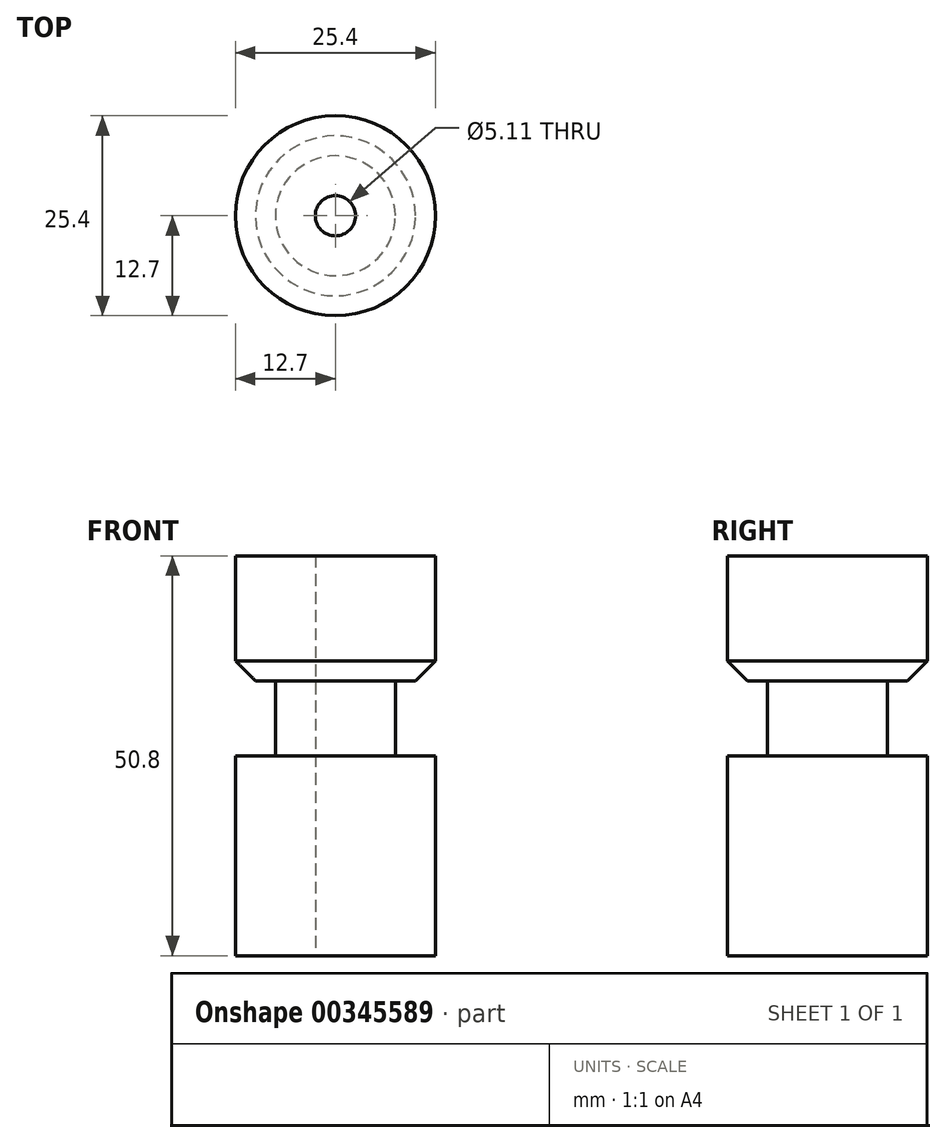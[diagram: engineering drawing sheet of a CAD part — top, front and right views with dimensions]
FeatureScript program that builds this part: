
annotation { "Feature Type Name" : "Feature", "Feature Type Description" : "" }
export const myFeature = defineFeature(function(context is Context, id is Id, definition is map)
    precondition{}
    {
        {
            var Q0;
            Q0=qCreatedBy(makeId("Top.planeOp"),FACE);
            var sketch = newSketch(context, id + "F0", { "sketchPlane" : qUnion([Q0])});
            skCircle(sketch, "E0", {"center": v(0, 0) * mm, "radius": 12.7 * mm});
            skSolve(sketch);
        }
        {
            var Q0;
            Q0 = qSketchRegion(id + "F0", true);
            extrude(context, id + "F1", {"entities" : qUnion([Q0]), "depth" : 50.8 * mm});
        }
        {
            var Q0;
            Q0=qCreatedBy(makeId("Right.planeOp"),FACE);
            var sketch = newSketch(context, id + "F2", { "sketchPlane" : qUnion([Q0])});
            skLineSegment(sketch, "E1.bottom", {"start": v(-7.62, 25.4) * mm, "end": v(-12.7, 25.4) * mm});
            skLineSegment(sketch, "E1.top", {"start": v(-7.62, 34.93) * mm, "end": v(-12.7, 34.93) * mm});
            skLineSegment(sketch, "E1.left", {"start": v(-7.62, 25.4) * mm, "end": v(-7.62, 34.93) * mm});
            skLineSegment(sketch, "E1.right", {"start": v(-12.7, 25.4) * mm, "end": v(-12.7, 34.93) * mm});
            skLineSegment(sketch, "E2", {"start": v(0, 0) * mm, "end": v(-30.16, 0) * mm});
            skLineSegment(sketch, "E3", {"start": v(-30.16, 0) * mm, "end": v(0, 0) * mm});
            skLineSegment(sketch, "E4", {"start": v(0, 102.3) * mm, "end": v(0, 0) * mm});
            skSolve(sketch);
        }
        {
            var Q0;
            Q0 = qSketchRegion(id + "F2", true);
            var Q1;
            Q1=sQuery(id+"F2.wireOp",EDGE,"E4");
            revolve(context, id + "F3", {"operationType" : NewBodyOperationType.REMOVE, "entities" : qUnion([Q0]), "axis" : qUnion([Q1]), "revolveType" : RevolveType.FULL, "oppositeDirection" : true});
        }
        {
            var Q0;
            Q0=makeQuery(id+"F3.boolean.opBoolean","COPY",EDGE,{"derivedFrom":makeQuery(id+"F3.opRevolve","SWEPT_EDGE",EDGE,{"disambiguationData":[OSD([sQuery(id+"F2.wireOp",EDGE,"E1.bottom"),sQuery(id+"F2.wireOp",EDGE,"E1.right")])]})});
            var Q1;
            Q1=makeQuery(id+"F3.boolean.opBoolean","COPY",EDGE,{"derivedFrom":makeQuery(id+"F3.opRevolve","SWEPT_EDGE",EDGE,{"disambiguationData":[OSD([sQuery(id+"F2.wireOp",EDGE,"E1.top"),sQuery(id+"F2.wireOp",EDGE,"E1.right")])]})});
            chamfer(context, id + "F4", {"entities" : qUnion([Q0, Q1]), "width" : 2.54 * mm, "tangentPropagation" : true});
        }
        {
            var Q0;
            Q0=qCreatedBy(makeId("Top.planeOp"),FACE);
            var sketch = newSketch(context, id + "F5", { "sketchPlane" : qUnion([Q0])});
            skPoint(sketch, "E5", {"position": v(0, 0) * mm});
            skSolve(sketch);
        }
        {
            var Q0;
            Q0=sQuery(id+"F5.wireOp",VERTEX,"E5");
            var Q1;
            Q1=makeQuery(id+"F1.opExtrude","SWEPT_BODY",BODY,{"disambiguationData":[OSD([sQuery(id+"F0.wireOp",EDGE,"E0")])]});
            hole(context, id + "F6", {"style" : HoleStyle.SIMPLE, "endStyle" : HoleEndStyle.THROUGH, "oppositeDirection" : true, "standardTappedOrClearance" : lookupTablePath({ "standard" : "ANSI", "fit" : "Normal (ASME)", "engagement" : "75%", "pitch" : "20 tpi", "size" : "1/4", "type" : "Tapped" }), "standardBlindInLast" : lookupTablePath({ "fit" : "Free", "standard" : "ANSI", "engagement" : "75%", "pitch" : "20 tpi", "size" : "1/4", "type" : "Tapped" }), "holeDiameter" : 5.1 * mm, "showTappedDepth" : true, "isTappedThrough" : true, "tappedDepth" : 12.7 * mm, "tapClearance" : 3, "locations" : qUnion([Q0]), "scope" : qUnion([Q1]), "majorDiameter" : 6.35 * mm});
        }
    });
